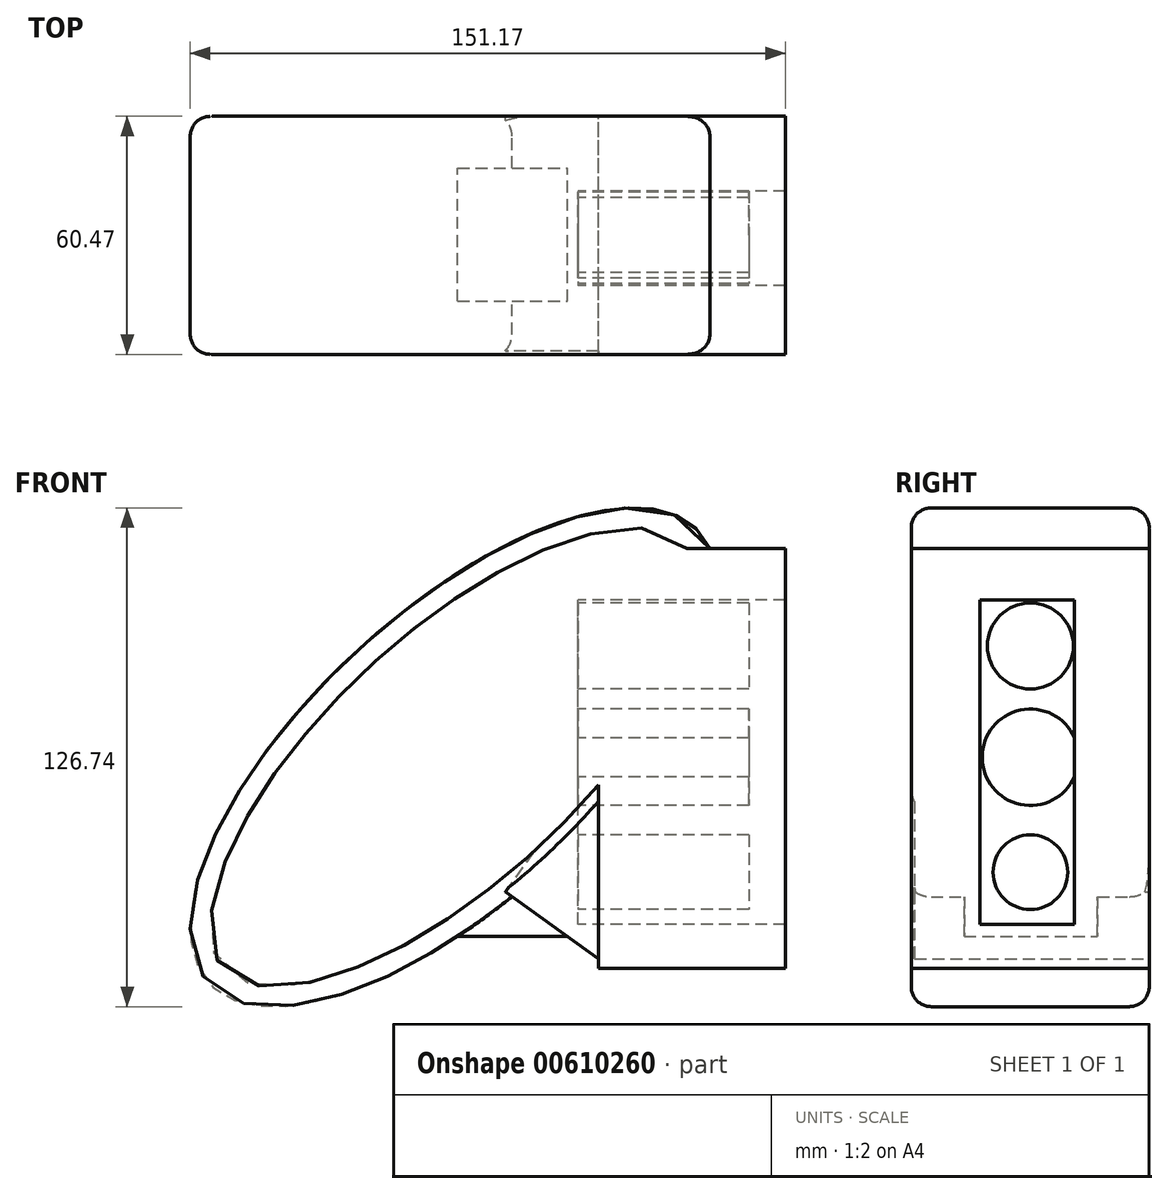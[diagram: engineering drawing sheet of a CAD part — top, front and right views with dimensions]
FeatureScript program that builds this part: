
annotation { "Feature Type Name" : "Feature", "Feature Type Description" : "" }
export const myFeature = defineFeature(function(context is Context, id is Id, definition is map)
    precondition{}
    {
        {
            var Q0;
            Q0=qCreatedBy(makeId("Front.planeOp"),FACE);
            var sketch = newSketch(context, id + "F0", { "sketchPlane" : qUnion([Q0])});
            skEllipse(sketch, "E0", {"center": v(0, 0) * mm, "majorRadius": 84.65 * mm, "minorRadius": 36.5 * mm, "majorAxis": v(0.73, 0.68)});
            skSolve(sketch);
        }
        {
            var Q0;
            Q0=makeQuery(id+"F0.imprint","IMPRINT",FACE,{"disambiguationData":[TD([[makeQuery(id+"F0.imprint","IMPRINT",EDGE,{"derivedFrom":sQuery(id+"F0.wireOp",EDGE,"E0")}),1.0]])]});
            extrude(context, id + "F1", {"entities" : qUnion([Q0]), "depth" : 60.46 * mm, "offsetDistance" : 25.4 * mm});
        }
        {
            var Q0;
            Q0=makeQuery(id+"F1.opExtrude","SWEPT_FACE",FACE,{"disambiguationData":[OSD([sQuery(id+"F0.wireOp",EDGE,"E0")])]});
            var Q1;
            Q1=makeQuery(id+"F1.opExtrude","CAP_FACE",FACE,{"disambiguationData":[OSD([sQuery(id+"F0.wireOp",EDGE,"E0")])],"isStart":false});
            fillet(context, id + "F2", {"entities" : qUnion([Q0, Q1]), "radius" : 5.08 * mm, "tangentPropagation" : true, "allowEdgeOverflow" : false});
        }
        {
            var Q0;
            Q0=qCreatedBy(makeId("Front.planeOp"),FACE);
            var sketch = newSketch(context, id + "F3", { "sketchPlane" : qUnion([Q0])});
            skLineSegment(sketch, "E1.bottom", {"start": v(84.2, 53.08) * mm, "end": v(36.75, 53.08) * mm});
            skLineSegment(sketch, "E1.top", {"start": v(84.2, -53.69) * mm, "end": v(36.75, -53.69) * mm});
            skLineSegment(sketch, "E1.left", {"start": v(84.2, 53.08) * mm, "end": v(84.2, -53.69) * mm});
            skLineSegment(sketch, "E1.right", {"start": v(36.75, 53.08) * mm, "end": v(36.75, -53.69) * mm});
            skSolve(sketch);
        }
        {
            var Q0;
            Q0=makeQuery(id+"F3.imprint","IMPRINT",FACE,{"disambiguationData":[TD([[makeQuery(id+"F3.imprint","IMPRINT",EDGE,{"derivedFrom":sQuery(id+"F3.wireOp",EDGE,"E1.bottom")}),1.0]])]});
            extrude(context, id + "F4", {"entities" : qUnion([Q0]), "operationType" : NewBodyOperationType.ADD, "depth" : 60.47 * mm, "offsetDistance" : 25.4 * mm});
        }
        {
            var Q0;
            Q0=qCreatedBy(makeId("Front.planeOp"),FACE);
            var sketch = newSketch(context, id + "F5", { "sketchPlane" : qUnion([Q0])});
            skLineSegment(sketch, "E2", {"start": v(37.82, -51.94) * mm, "end": v(13.12, -34.22) * mm});
            skLineSegment(sketch, "E3", {"start": v(13.12, -34.22) * mm, "end": v(37.68, 0) * mm});
            skLineSegment(sketch, "E4", {"start": v(37.68, 0) * mm, "end": v(37.82, -51.94) * mm});
            skSolve(sketch);
        }
        {
            var Q0;
            Q0 = qSketchRegion(id + "F5", true);
            var Q1;
            Q1=makeQuery(id+"F5.imprint","IMPRINT",FACE,{"disambiguationData":[TD([[makeQuery(id+"F5.imprint","IMPRINT",EDGE,{"derivedFrom":sQuery(id+"F5.wireOp",EDGE,"E2")}),-1.0]])]});
            extrude(context, id + "F6", {"entities" : qUnion([Q0, Q1]), "operationType" : NewBodyOperationType.ADD, "depth" : 59.66 * mm, "offsetDistance" : 25.4 * mm});
        }
        {
            var Q0;
            Q0=qCreatedBy(makeId("Right.planeOp"),FACE);
            var sketch = newSketch(context, id + "F7", { "sketchPlane" : qUnion([Q0])});
            skLineSegment(sketch, "E5.bottom", {"start": v(-42.98, 39.9) * mm, "end": v(-18.98, 39.9) * mm});
            skLineSegment(sketch, "E5.top", {"start": v(-42.98, -42.42) * mm, "end": v(-18.98, -42.42) * mm});
            skLineSegment(sketch, "E5.left", {"start": v(-42.98, 39.9) * mm, "end": v(-42.98, -42.42) * mm});
            skLineSegment(sketch, "E5.right", {"start": v(-18.98, 39.9) * mm, "end": v(-18.98, -42.42) * mm});
            skSolve(sketch);
        }
        {
            var Q0;
            Q0 = qSketchRegion(id + "F7", true);
            extrude(context, id + "F8", {"entities" : qUnion([Q0]), "operationType" : NewBodyOperationType.REMOVE, "depth" : 127.1 * mm, "offsetDistance" : 25.4 * mm});
        }
        {
            var Q0;
            Q0=qCreatedBy(makeId("Top.planeOp"),FACE);
            var sketch = newSketch(context, id + "F9", { "sketchPlane" : qUnion([Q0])});
            skLineSegment(sketch, "E6.bottom", {"start": v(0, -46.97) * mm, "end": v(31.56, -46.97) * mm});
            skLineSegment(sketch, "E6.top", {"start": v(0, -13.15) * mm, "end": v(31.56, -13.15) * mm});
            skLineSegment(sketch, "E6.left", {"start": v(0, -46.97) * mm, "end": v(0, -13.15) * mm});
            skLineSegment(sketch, "E6.right", {"start": v(31.56, -46.97) * mm, "end": v(31.56, -13.15) * mm});
            skSolve(sketch);
        }
        {
            var Q0;
            Q0 = qSketchRegion(id + "F9", true);
            var Q1;
            Q1=makeQuery(id+"F9.imprint","IMPRINT",FACE,{"disambiguationData":[TD([[makeQuery(id+"F9.imprint","IMPRINT",EDGE,{"derivedFrom":sQuery(id+"F9.wireOp",EDGE,"E6.bottom")}),1.0]])]});
            extrude(context, id + "F10", {"entities" : qUnion([Q0, Q1]), "operationType" : NewBodyOperationType.ADD, "endBound" : BoundingType.SYMMETRIC, "depth" : 91.05 * mm, "offsetDistance" : 25.4 * mm});
        }
        {
            var Q0;
            Q0=qCreatedBy(makeId("Right.planeOp"),FACE);
            var sketch = newSketch(context, id + "F11", { "sketchPlane" : qUnion([Q0])});
            skCircle(sketch, "E7", {"center": v(-30.2, 28.28) * mm, "radius": 10.93 * mm});
            skCircle(sketch, "E8", {"center": v(-30.2, 0) * mm, "radius": 12.25 * mm});
            skCircle(sketch, "E9", {"center": v(-30.2, -29.2) * mm, "radius": 9.48 * mm});
            skSolve(sketch);
        }
        {
            var Q0;
            Q0 = qSketchRegion(id + "F11", true);
            extrude(context, id + "F12", {"entities" : qUnion([Q0]), "operationType" : NewBodyOperationType.ADD, "depth" : 75 * mm, "offsetDistance" : 25.4 * mm});
        }
    });
